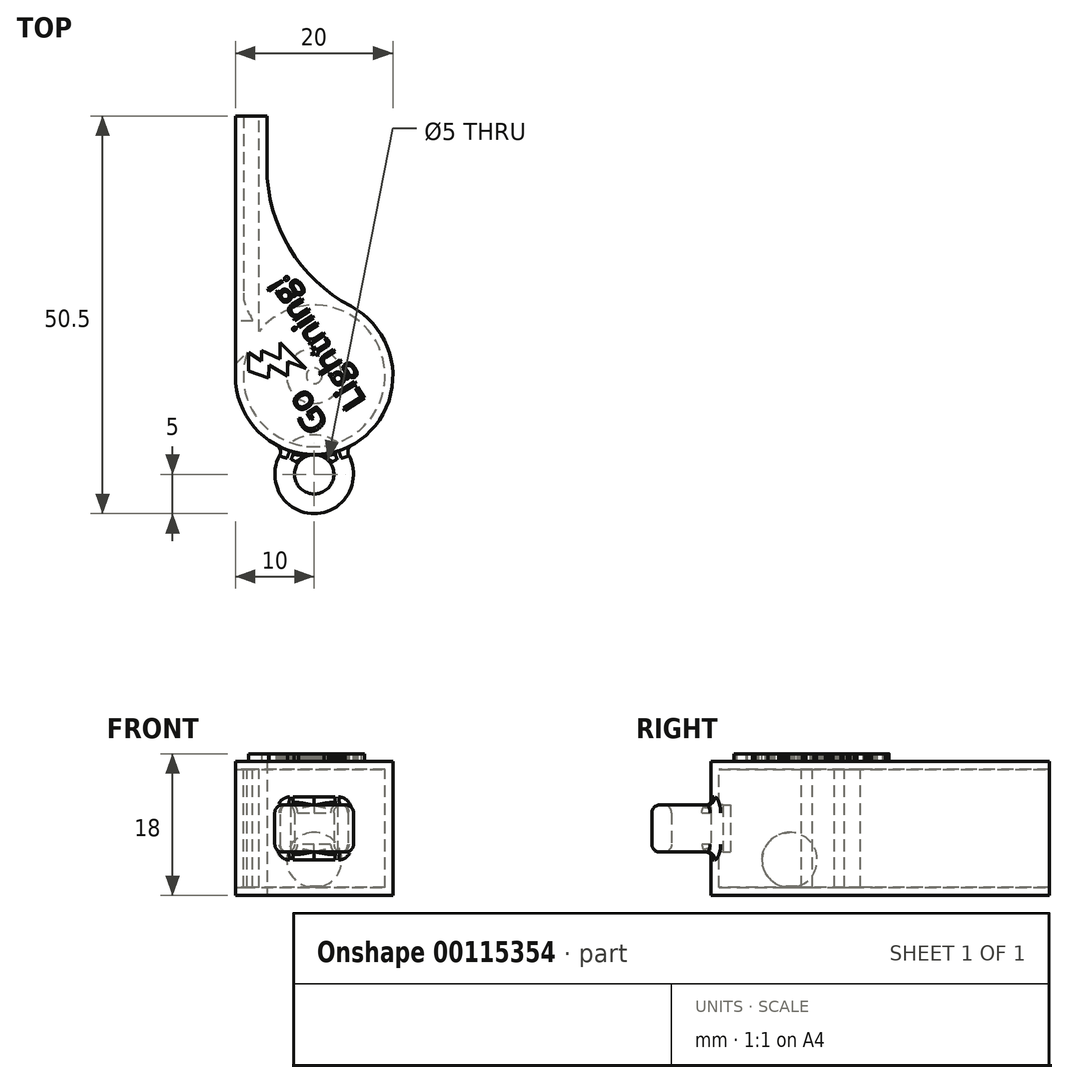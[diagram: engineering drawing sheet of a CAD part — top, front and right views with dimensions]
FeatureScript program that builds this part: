
annotation { "Feature Type Name" : "Feature", "Feature Type Description" : "" }
export const myFeature = defineFeature(function(context is Context, id is Id, definition is map)
    precondition{}
    {
        {
            var Q0;
            Q0=qCreatedBy(makeId("Top.planeOp"),FACE);
            var sketch = newSketch(context, id + "F0", { "sketchPlane" : qUnion([Q0])});
            skArc(sketch, "E0.0.4", {"start": v(-10, 0) * mm, "mid": v(5.16, -8.56) * mm, "end": v(4.67, 8.84) * mm});
            skLineSegment(sketch, "E0.0.3", {"start": v(-10, 33) * mm, "end": v(-10, 0) * mm});
            skLineSegment(sketch, "E0.0.2", {"start": v(-6, 33) * mm, "end": v(-10, 33) * mm});
            skLineSegment(sketch, "E0.0.1", {"start": v(-6, 26.53) * mm, "end": v(-6, 33) * mm});
            skArc(sketch, "E0.0.0", {"start": v(4.67, 8.84) * mm, "mid": v(-3.13, 16.2) * mm, "end": v(-6, 26.53) * mm});
            skSolve(sketch);
        }
        {
            var Q0;
            Q0=makeQuery(id+"F0.imprint","IMPRINT",FACE,{"disambiguationData":[TD([[makeQuery(id+"F0.imprint","IMPRINT",EDGE,{"derivedFrom":sQuery(id+"F0.wireOp",EDGE,"E0.0.4")}),1.0]])]});
            extrude(context, id + "F1", {"entities" : qUnion([Q0]), "endBound" : BoundingType.SYMMETRIC, "depth" : 17 * mm});
        }
        {
            var Q0;
            Q0=qCreatedBy(makeId("Top.planeOp"),FACE);
            var sketch = newSketch(context, id + "F2", { "sketchPlane" : qUnion([Q0])});
            skLineSegment(sketch, "E1.0", {"start": v(-9, 33) * mm, "end": v(-9, 10.5) * mm});
            skLineSegment(sketch, "E2.0", {"start": v(-7, 5.66) * mm, "end": v(-7, 33) * mm});
            skArc(sketch, "E3.0", {"start": v(-8.53, 2.87) * mm, "mid": v(7.89, -4.33) * mm, "end": v(-7, 5.66) * mm});
            skLineSegment(sketch, "E4.0", {"start": v(-10, 1.48) * mm, "end": v(-8.58, 2.9) * mm});
            skArc(sketch, "E5.0", {"start": v(-8.03, 7.54) * mm, "mid": v(-8.75, 8.94) * mm, "end": v(-9, 10.5) * mm});
            skArc(sketch, "E6.0", {"start": v(-7.8, 6.95) * mm, "mid": v(-7.87, 7.26) * mm, "end": v(-8.03, 7.54) * mm});
            skLineSegment(sketch, "E7.0", {"start": v(-7.8, 6.95) * mm, "end": v(-10, 6.95) * mm});
            skLineSegment(sketch, "E8", {"start": v(-7, 33) * mm, "end": v(-9, 33) * mm});
            skLineSegment(sketch, "E9", {"start": v(-10, 6.95) * mm, "end": v(-10, 1.48) * mm});
            skPoint(sketch, "E10.visualSharp", {"position": v(-8.49, 3) * mm});
            skArc(sketch, "E10.filletArc", {"start": v(-8.53, 2.87) * mm, "mid": v(-8.54, 2.9) * mm, "end": v(-8.58, 2.9) * mm});
            skSolve(sketch);
        }
        {
            var Q0;
            Q0=makeQuery(id+"F2.imprint","IMPRINT",FACE,{"disambiguationData":[TD([[makeQuery(id+"F2.imprint","IMPRINT",EDGE,{"derivedFrom":sQuery(id+"F2.wireOp",EDGE,"E1.0")}),1.0]])]});
            extrude(context, id + "F3", {"entities" : qUnion([Q0]), "operationType" : NewBodyOperationType.REMOVE, "endBound" : BoundingType.SYMMETRIC, "oppositeDirection" : true, "depth" : 15 * mm});
        }
        {
            var Q0;
            Q0=qCreatedBy(makeId("Right.planeOp"),FACE);
            var sketch = newSketch(context, id + "F4", { "sketchPlane" : qUnion([Q0])});
            skArc(sketch, "E11", {"start": v(0, -7.5) * mm, "mid": v(3.5, -4) * mm, "end": v(0, -0.5) * mm});
            skLineSegment(sketch, "E12.0", {"start": v(-9, -7.5) * mm, "end": v(9, -7.5) * mm, "construction": true});
            skLineSegment(sketch, "E13", {"start": v(0, 3.94) * mm, "end": v(0, -16.8) * mm, "construction": true});
            skLineSegment(sketch, "E14", {"start": v(0, -7.5) * mm, "end": v(0, -0.5) * mm});
            skSolve(sketch);
        }
        {
            var Q0;
            Q0=makeQuery(id+"F4.imprint","IMPRINT",FACE,{"disambiguationData":[TD([[makeQuery(id+"F4.imprint","IMPRINT",EDGE,{"derivedFrom":sQuery(id+"F4.wireOp",EDGE,"E11")}),1.0]])]});
            var Q1;
            Q1=sQuery(id+"F4.wireOp",EDGE,"E11");
            var Q2;
            Q2=sQuery(id+"F4.wireOp",EDGE,"E13");
            revolve(context, id + "F5", {"entities" : qUnion([Q0]), "surfaceEntities" : qUnion([Q1]), "axis" : qUnion([Q2]), "revolveType" : RevolveType.FULL});
        }
        {
            var Q0;
            Q0=qCreatedBy(makeId("Top.planeOp"),FACE);
            var sketch = newSketch(context, id + "F6", { "sketchPlane" : qUnion([Q0])});
            skArc(sketch, "E15", {"start": v(-3.8, -9.25) * mm, "mid": v(0, -17.5) * mm, "end": v(3.8, -9.25) * mm});
            skCircle(sketch, "E16", {"center": v(0, -12.5) * mm, "radius": 2.5 * mm});
            skPoint(sketch, "E17.orphan", {"position": v(-10, 0) * mm});
            skPoint(sketch, "E18.orphan", {"position": v(4.67, 8.84) * mm});
            skArc(sketch, "E19", {"start": v(-3.8, -9.25) * mm, "mid": v(0, -7.5) * mm, "end": v(3.8, -9.25) * mm});
            skSolve(sketch);
        }
        {
            var Q0;
            {var subQ1=sQuery(id+"F6.wireOp",EDGE,"E15");Q0=makeQuery(id+"F6.imprint","IMPRINT",FACE,{"disambiguationData":[TD([[makeQuery(id+"F6.imprint","IMPRINT",EDGE,{"derivedFrom":subQ1}),1.0]])]});}
            extrude(context, id + "F7", {"entities" : qUnion([Q0]), "operationType" : NewBodyOperationType.ADD, "endBound" : BoundingType.SYMMETRIC, "depth" : 6 * mm});
        }
        {
            var Q0;
            {var subQ0=sQuery(id+"F6.wireOp",EDGE,"E15");var subQ1=sQuery(id+"F6.wireOp",EDGE,"E19");Q0=makeQuery(id+"F7.boolean.opBoolean","SPLIT",FACE,{"disambiguationData":[TD([makeQuery(id+"F1.opExtrude","SWEPT_FACE",FACE,{"disambiguationData":[OSD([sQuery(id+"F0.wireOp",EDGE,"E0.0.4")])]})])],"derivedFrom":makeQuery(id+"F7.opExtrude","SWEPT_FACE",FACE,{"disambiguationData":[OSD([subQ0,subQ1])]})});}
            var Q1;
            {var subQ0=sQuery(id+"F6.wireOp",EDGE,"E15");var subQ1=sQuery(id+"F6.wireOp",EDGE,"E16");var subQ2=sQuery(id+"F6.wireOp",EDGE,"E19");Q1=makeQuery(id+"F7.boolean.opBoolean","SPLIT",FACE,{"disambiguationData":[TD([makeQuery(id+"F1.opExtrude","SWEPT_FACE",FACE,{"disambiguationData":[OSD([sQuery(id+"F0.wireOp",EDGE,"E0.0.4")])]})])],"derivedFrom":makeQuery(id+"F7.opExtrude","CAP_FACE",FACE,{"disambiguationData":[OSD([subQ0,subQ1,subQ2])],"isStart":false})});}
            var Q2;
            {var subQ0=sQuery(id+"F6.wireOp",EDGE,"E15");var subQ1=sQuery(id+"F6.wireOp",EDGE,"E16");var subQ2=sQuery(id+"F6.wireOp",EDGE,"E19");Q2=makeQuery(id+"F7.boolean.opBoolean","SPLIT",FACE,{"disambiguationData":[TD([makeQuery(id+"F1.opExtrude","SWEPT_FACE",FACE,{"disambiguationData":[OSD([sQuery(id+"F0.wireOp",EDGE,"E0.0.4")])]})])],"derivedFrom":makeQuery(id+"F7.opExtrude","CAP_FACE",FACE,{"disambiguationData":[OSD([subQ0,subQ1,subQ2])],"isStart":true})});}
            var Q3;
            Q3=makeQuery(id+"F3.boolean.opBoolean","COPY",EDGE,{"derivedFrom":makeQuery(id+"F3.opExtrude","CAP_EDGE",EDGE,{"disambiguationData":[OSD([sQuery(id+"F2.wireOp",EDGE,"E8")])],"isStart":true})});
            var Q4;
            Q4=makeQuery(id+"F3.boolean.opBoolean","COPY",EDGE,{"derivedFrom":makeQuery(id+"F3.opExtrude","SWEPT_EDGE",EDGE,{"disambiguationData":[OSD([sQuery(id+"F2.wireOp",EDGE,"E1.0"),sQuery(id+"F2.wireOp",EDGE,"E8")])]})});
            var Q5;
            Q5=makeQuery(id+"F3.boolean.opBoolean","COPY",EDGE,{"derivedFrom":makeQuery(id+"F3.opExtrude","SWEPT_EDGE",EDGE,{"disambiguationData":[OSD([sQuery(id+"F2.wireOp",EDGE,"E2.0"),sQuery(id+"F2.wireOp",EDGE,"E8")])]})});
            var Q6;
            Q6=makeQuery(id+"F3.boolean.opBoolean","COPY",EDGE,{"derivedFrom":makeQuery(id+"F3.opExtrude","CAP_EDGE",EDGE,{"disambiguationData":[OSD([sQuery(id+"F2.wireOp",EDGE,"E8")])],"isStart":false})});
            fillet(context, id + "F8", {"entities" : qUnion([Q0, Q1, Q2, Q3, Q4, Q5, Q6]), "radius" : 1 * mm, "tangentPropagation" : true, "allowEdgeOverflow" : false});
        }
        {
            var Q0;
            Q0=makeQuery(id+"F1.opExtrude","CAP_FACE",FACE,{"disambiguationData":[OSD([sQuery(id+"F0.wireOp",EDGE,"E0.0.4"),sQuery(id+"F0.wireOp",EDGE,"E0.0.3"),sQuery(id+"F0.wireOp",EDGE,"E0.0.2"),sQuery(id+"F0.wireOp",EDGE,"E0.0.1"),sQuery(id+"F0.wireOp",EDGE,"E0.0.0")])],"isStart":false});
            var sketch = newSketch(context, id + "F9", { "sketchPlane" : qUnion([Q0])});
            skText(sketch, "E20", { "text": "Go\nLightning!", "fontName": "OpenSans-Regular.ttf"});
            const initialGuessF9  = {"E20": [0.00187, -0.00618, -0.53827, 0.84277, 0.003]};
            skSetInitialGuess(sketch, initialGuessF9);
            skSolve(sketch);
        }
        {
            var Q0;
            Q0=makeQuery(id+"F3.boolean.opBoolean","COPY",FACE,{"derivedFrom":makeQuery(id+"F3.opExtrude","CAP_FACE",FACE,{"disambiguationData":[OSD([sQuery(id+"F2.wireOp",EDGE,"E1.0"),sQuery(id+"F2.wireOp",EDGE,"E2.0"),sQuery(id+"F2.wireOp",EDGE,"E3.0"),sQuery(id+"F2.wireOp",EDGE,"E4.0"),sQuery(id+"F2.wireOp",EDGE,"E5.0"),sQuery(id+"F2.wireOp",EDGE,"E6.0"),sQuery(id+"F2.wireOp",EDGE,"E7.0"),sQuery(id+"F2.wireOp",EDGE,"E8"),sQuery(id+"F2.wireOp",EDGE,"E9"),sQuery(id+"F2.wireOp",EDGE,"E10.filletArc")])],"isStart":false})});
            var sketch = newSketch(context, id + "F10", { "sketchPlane" : qUnion([Q0])});
            skCircle(sketch, "E21", {"center": v(0, 0) * mm, "radius": 1 * mm});
            skSolve(sketch);
        }
        {
            var Q0;
            Q0=qSketchRegion(id+"F10",true);
            extrude(context, id + "F11", {"entities" : qUnion([Q0]), "operationType" : NewBodyOperationType.ADD, "depth" : 2 * mm});
        }
        {
            var Q0;
            Q0 = qSketchRegion(id + "F9", true);
            extrude(context, id + "F12", {"entities" : qUnion([Q0]), "operationType" : NewBodyOperationType.ADD, "depth" : 1 * mm});
        }
        {
            var Q0;
            {var subQ1=sQuery(id+"F0.wireOp",EDGE,"E0.0.4");var subQ2=sQuery(id+"F0.wireOp",EDGE,"E0.0.0");var subQ3=sQuery(id+"F0.wireOp",EDGE,"E0.0.3");var subQ4=sQuery(id+"F0.wireOp",EDGE,"E0.0.1");Q0=makeQuery(id+"F12.boolean.opBoolean","SPLIT",FACE,{"disambiguationData":[TD([makeQuery(id+"F1.opExtrude","SWEPT_FACE",FACE,{"disambiguationData":[OSD([subQ1])]})])],"derivedFrom":makeQuery(id+"F1.opExtrude","CAP_FACE",FACE,{"disambiguationData":[OSD([subQ1,subQ3,sQuery(id+"F0.wireOp",EDGE,"E0.0.2"),subQ4,subQ2])],"isStart":false})});}
            var sketch = newSketch(context, id + "F13", { "sketchPlane" : qUnion([Q0])});
            skLineSegment(sketch, "E22", {"start": v(-5.77, -0.3) * mm, "end": v(-5.7, 1.4) * mm});
            skLineSegment(sketch, "E23", {"start": v(-5.7, 1.4) * mm, "end": v(-3.38, 0) * mm});
            skLineSegment(sketch, "E24", {"start": v(-3.38, 1.81) * mm, "end": v(-1.05, 0.93) * mm});
            skLineSegment(sketch, "E25", {"start": v(-1.05, 0.93) * mm, "end": v(-4.34, 4.22) * mm});
            skLineSegment(sketch, "E26", {"start": v(-4.34, 4.22) * mm, "end": v(-4.34, 2.13) * mm});
            skLineSegment(sketch, "E27", {"start": v(-4.34, 2.13) * mm, "end": v(-6.7, 3.25) * mm});
            skLineSegment(sketch, "E28", {"start": v(-6.7, 3.25) * mm, "end": v(-6.7, 1.87) * mm});
            skLineSegment(sketch, "E29", {"start": v(-3.38, 0) * mm, "end": v(-3.38, 1.81) * mm});
            skPoint(sketch, "E30.orphan", {"position": v(-8.36, 0) * mm});
            skPoint(sketch, "E31.start.orphan", {"position": v(-7.15, 0) * mm});
            skLineSegment(sketch, "E32", {"start": v(-8.36, 2.94) * mm, "end": v(-6.7, 1.87) * mm});
            skLineSegment(sketch, "E33", {"start": v(-8.36, 0.64) * mm, "end": v(-8.36, 2.94) * mm});
            skLineSegment(sketch, "E34", {"start": v(-8.36, 0.64) * mm, "end": v(-5.77, -0.3) * mm});
            skSolve(sketch);
        }
        {
            var Q0;
            Q0=makeQuery(id+"F13.imprint","IMPRINT",FACE,{"disambiguationData":[TD([[makeQuery(id+"F13.imprint","IMPRINT",EDGE,{"derivedFrom":sQuery(id+"F13.wireOp",EDGE,"E22")}),1.0]])]});
            extrude(context, id + "F14", {"entities" : qUnion([Q0]), "operationType" : NewBodyOperationType.ADD, "depth" : 1 * mm});
        }
    });
